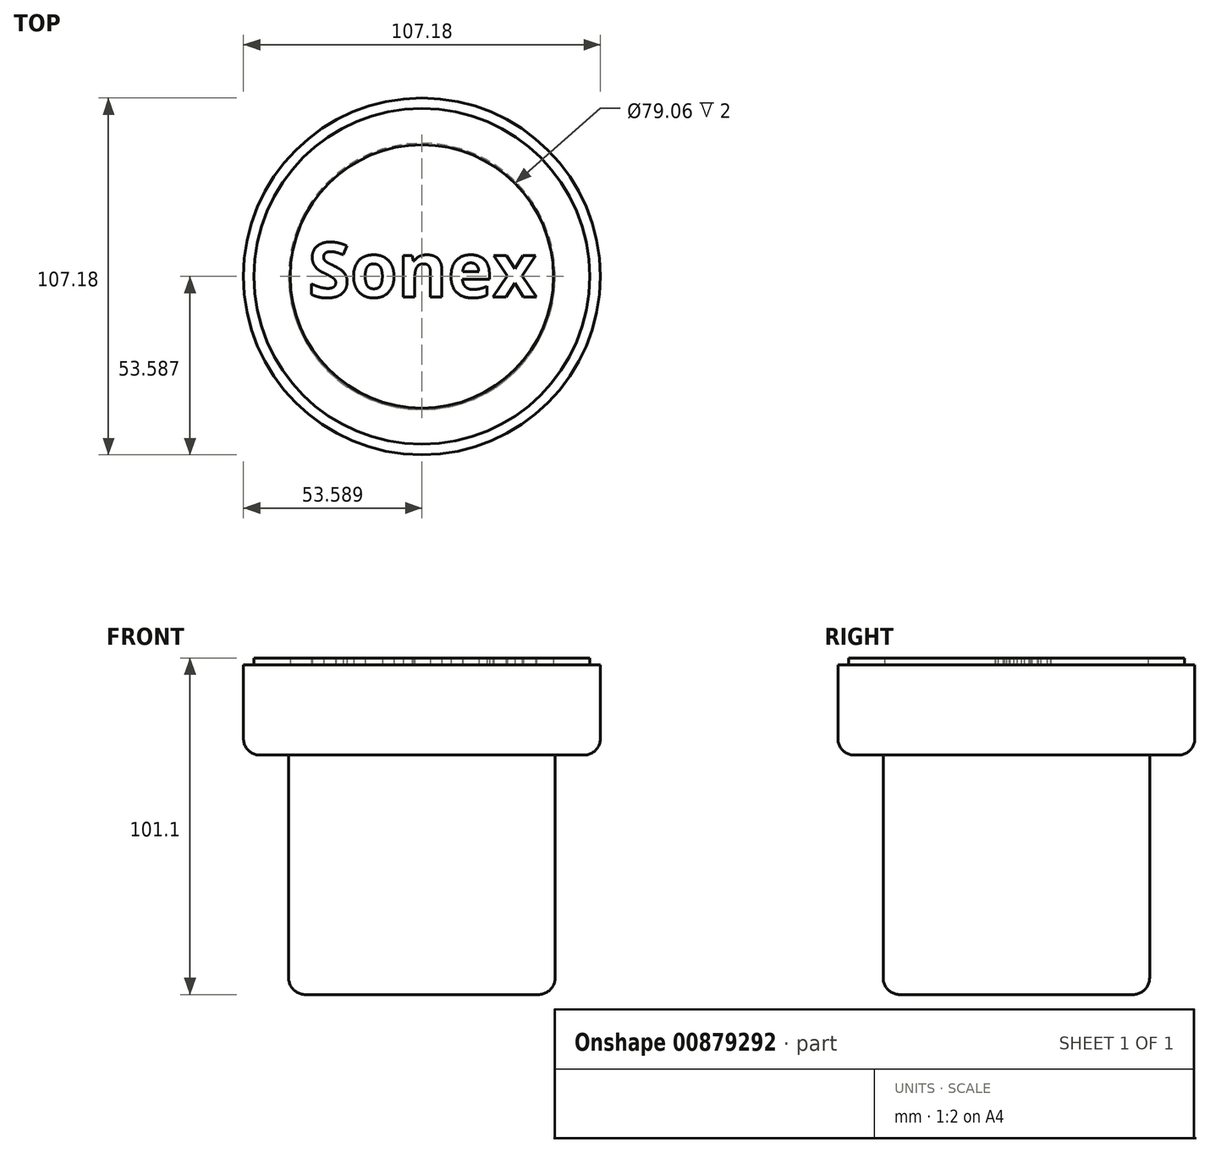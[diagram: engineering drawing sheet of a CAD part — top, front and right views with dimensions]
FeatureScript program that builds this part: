
annotation { "Feature Type Name" : "Feature", "Feature Type Description" : "" }
export const myFeature = defineFeature(function(context is Context, id is Id, definition is map)
    precondition{}
    {
        {
            var Q0;
            Q0=qCreatedBy(makeId("Top.planeOp"),FACE);
            var sketch = newSketch(context, id + "F0", { "sketchPlane" : qUnion([Q0])});
            skCircle(sketch, "E0", {"center": v(-1.45, 0.68) * mm, "radius": 53.59 * mm});
            skSolve(sketch);
        }
        {
            var Q0;
            Q0 = qSketchRegion(id + "F0", true);
            extrude(context, id + "F1", {"entities" : qUnion([Q0]), "depth" : 27.1 * mm, "offsetDistance" : 25 * mm});
        }
        {
            var Q0;
            Q0=makeQuery(id+"F1.opExtrude","CAP_FACE",FACE,{"disambiguationData":[OSD([sQuery(id+"F0.wireOp",EDGE,"E0")])],"isStart":false});
            var sketch = newSketch(context, id + "F2", { "sketchPlane" : qUnion([Q0])});
            skCircle(sketch, "E1", {"center": v(-1.45, 0.68) * mm, "radius": 50.43 * mm});
            skCircle(sketch, "E2.0", {"center": v(-1.45, 0.68) * mm, "radius": 39.53 * mm});
            skSolve(sketch);
        }
        {
            var Q0;
            Q0 = qSketchRegion(id + "F2", true);
            extrude(context, id + "F3", {"entities" : qUnion([Q0]), "operationType" : NewBodyOperationType.ADD, "depth" : 2 * mm, "offsetDistance" : 25 * mm});
        }
        {
            var Q0;
            Q0=makeQuery(id+"F3.boolean.opBoolean","SPLIT",FACE,{"disambiguationData":[TD([makeQuery(id+"F3.opExtrude","SWEPT_FACE",FACE,{"disambiguationData":[OSD([sQuery(id+"F2.wireOp",EDGE,"E2.0")])]})])],"derivedFrom":makeQuery(id+"F1.opExtrude","CAP_FACE",FACE,{"disambiguationData":[OSD([sQuery(id+"F0.wireOp",EDGE,"E0")])],"isStart":false})});
            var sketch = newSketch(context, id + "F4", { "sketchPlane" : qUnion([Q0])});
            skText(sketch, "E3", { "text": "Sonex", "fontName": "NotoSans-Bold.ttf"});
            const initialGuessF4  = {"E3": [-0.03561, -0.00557, 1, 0, 0.0165]};
            skSetInitialGuess(sketch, initialGuessF4);
            skSolve(sketch);
        }
        {
            var Q0;
            Q0 = qSketchRegion(id + "F4", true);
            extrude(context, id + "F5", {"entities" : qUnion([Q0]), "operationType" : NewBodyOperationType.ADD, "depth" : 2.1 * mm, "offsetDistance" : 25 * mm});
        }
        {
            var Q0;
            Q0=makeQuery(id+"F1.opExtrude","CAP_EDGE",EDGE,{"disambiguationData":[OSD([sQuery(id+"F0.wireOp",EDGE,"E0")])],"isStart":true});
            fillet(context, id + "F6", {"entities" : qUnion([Q0]), "radius" : 5 * mm, "tangentPropagation" : true, "allowEdgeOverflow" : false});
        }
        {
            var Q0;
            Q0=makeQuery(id+"F1.opExtrude","CAP_FACE",FACE,{"disambiguationData":[OSD([sQuery(id+"F0.wireOp",EDGE,"E0")])],"isStart":true});
            var sketch = newSketch(context, id + "F7", { "sketchPlane" : qUnion([Q0])});
            skCircle(sketch, "E4", {"center": v(-1.45, -0.68) * mm, "radius": 40.01 * mm});
            skSolve(sketch);
        }
        {
            var Q0;
            Q0 = qSketchRegion(id + "F7", true);
            extrude(context, id + "F8", {"entities" : qUnion([Q0]), "operationType" : NewBodyOperationType.ADD, "depth" : 71.9 * mm, "offsetDistance" : 25 * mm});
        }
        {
            var Q0;
            Q0=makeQuery(id+"F8.opExtrude","CAP_EDGE",EDGE,{"disambiguationData":[OSD([sQuery(id+"F7.wireOp",EDGE,"E4")])],"isStart":false});
            fillet(context, id + "F9", {"entities" : qUnion([Q0]), "radius" : 5 * mm, "tangentPropagation" : true, "allowEdgeOverflow" : false});
        }
    });
